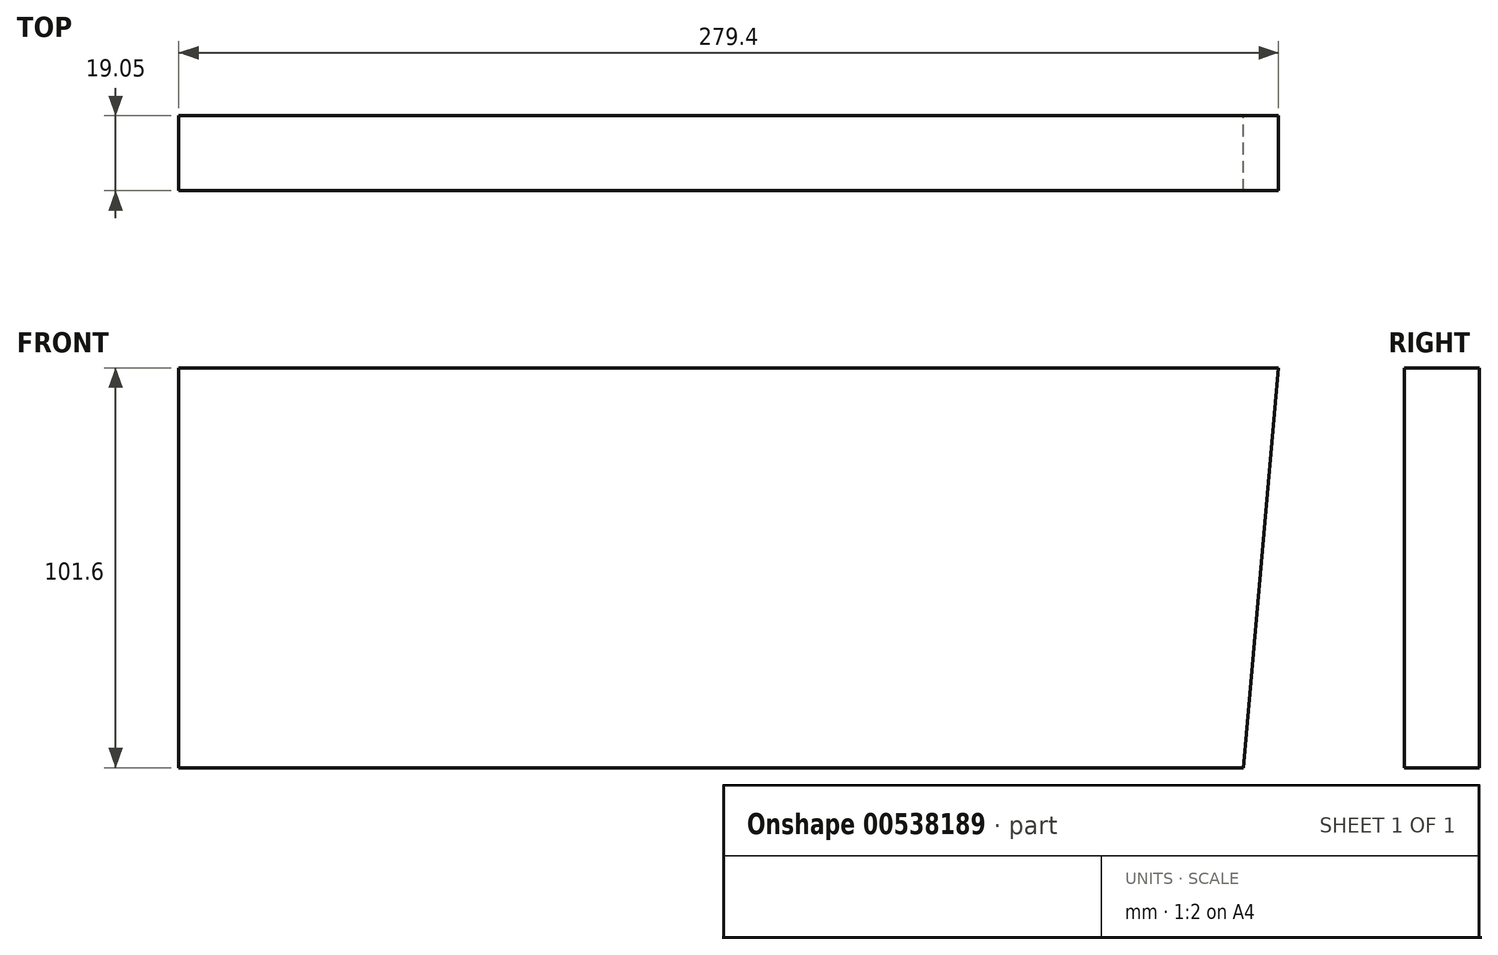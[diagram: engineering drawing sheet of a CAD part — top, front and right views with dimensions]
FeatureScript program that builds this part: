
annotation { "Feature Type Name" : "Feature", "Feature Type Description" : "" }
export const myFeature = defineFeature(function(context is Context, id is Id, definition is map)
    precondition{}
    {
        {
            var Q0;
            Q0=qCreatedBy(makeId("Front.planeOp"),FACE);
            var sketch = newSketch(context, id + "F0", { "sketchPlane" : qUnion([Q0])});
            skLineSegment(sketch, "E0.bottom", {"start": v(-152.42, 77.31) * mm, "end": v(126.98, 77.31) * mm});
            skLineSegment(sketch, "E0.top", {"start": v(-152.42, -24.29) * mm, "end": v(118.26, -24.29) * mm});
            skLineSegment(sketch, "E0.left", {"start": v(-152.42, 77.31) * mm, "end": v(-152.42, -24.29) * mm});
            skLineSegment(sketch, "E1", {"start": v(126.98, 77.31) * mm, "end": v(118.1, -24.29) * mm});
            skSolve(sketch);
        }
        {
            var Q0;
            Q0 = qSketchRegion(id + "F0", true);
            extrude(context, id + "F1", {"entities" : qUnion([Q0]), "depth" : 19.05 * mm, "offsetDistance" : 25.4 * mm});
        }
    });
